# Revit family: xZumtobel SUI DF9
name_source: partatom
category: Lighting Fixtures
revit_build: Autodesk Revit 2016 (Build: 20150220_1215(x64)
units: mm (PartAtom-declared; Revit-internal decimal feet)

## family parameters
Cut with Voids When Loaded = No
Host = Face
Light Source = Yes
OmniClass Number = 23.80.70.11
OmniClass Title = Luminaries for Internal Lighting
Part Type = Normal
Room Calculation Point = No
Round Connector Dimension = Use Diameter
Shared = No

## types (3) — shared parameters
Apparent Load = 36 VA
Assembly Code = D5020200
Color Filter = 16777215
Description = LED ceiling luminaire
Dimming Lamp Color Temperature Shift = <None>
Emit Shape Visible in Rendering = No
Emit from Rectangle Length = 50 mm  [stored 0.164042 ft]
Emit from Rectangle Width = 335 mm  [stored 1.09908 ft]
Height = 49 mm  [stored 0.160761 ft]
Lamp = LED
Length = 335 mm  [stored 1.09908 ft]
Manufacturer = Zumtobel Lighting
Tilt Angle = -90.00°
URL = http://www.zumtobel.com
Voltage = 230 V
Width = 50 mm  [stored 0.164042 ft]
zero-valued in all types: Default Elevation

## per-type parameters (varying)
| type | Model | Photometric Web File |
| SUI DF9 VFL | 60211002 | 60211002_(STD_LEO).IES |
| SUI DF9 FL | 60211001 | 60211001_(STD_LEO).IES |
| SUI DF9 WW | 60211004 | 60211004_(STD_LEO).IES |

note: [stored X ft] marks values corroborated as IEEE doubles in the binary element streams (Revit-internal decimal feet)

## geometry (parser evidence)
native form markers: Sweep x3
no freeform markers — native parametric forms only
